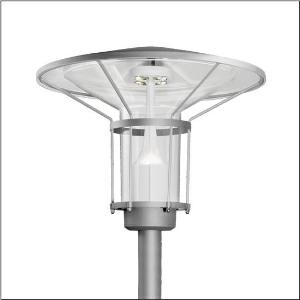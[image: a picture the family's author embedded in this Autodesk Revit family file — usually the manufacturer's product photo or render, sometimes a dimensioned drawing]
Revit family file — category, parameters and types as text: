
# Revit family: laterne_classic_iq___p1_0a_5xa5245ff14h_a382
name_source: partatom
category: Lighting Fixtures
units: mm (PartAtom-declared; Revit-internal decimal feet)

## family parameters
Cut with Voids When Loaded = No
Host = Face
Light Source = No
Part Type = Normal
Room Calculation Point = No
Round Connector Dimension = Use Diameter
Shared = No

## types (1)
- --- (1 x LED, 1360 lm, 10.5 W, 3000K)
    Apparent Load = 11 VA
    CIE Flux Codes = 30 61 91 96 100
    Color Rendering = 70
    Color Temperature = 3000K
    Default Elevation = 1800 mm
    Description = Lantern Classic iQ, mast luminaire, Module 540 iQ-SR, primary light control with 3 zone facetted reflector, of plastic, silver coated, highly specular, structured, primary optical cover: cover, of PMMA, transparent, light distribution: P1.0a, light emission: direct distribution, primary light characteristic: strongly asymmetric, installation type: post-top, LED, High Power LED, rated luminous flux: 1.360lm, luminous efficacy: 130lm/W, light colour: 730, colour temperature: 3000K, control gear: ECG iQ, control: Auto-Match, Temp-Guard, Lumen-Switch, Night-Set, Smart-Wire, Light-Fading, Desk-Remote (wireless, voltage-free reading and setting of iQ features in the workshop via application-optimized NFC function/RFID function), optimised constant luminous flux control (CLO 2.0), Street-Remote, presetting dimming logarithmic, with terminal, 6-pole, max. 2.5mm², mains connection: 230..240V, AC, 50/60Hz, start of lifetime: 11W, end of service life: 11W, reduction: 5W, luminaire housing, upper part, of glass-fibre reinforced polyester, coated, Siteco® metallic grey (DB 702S), diameter: 750mm, height: 596mm, spigot size: d x l = 76 x 70mm (post-top) | with reducer (optional accessory) 60 x 70mm, post-top mast mounting element, of diecast aluminium, coated, Siteco® metallic grey (DB 702S), Module 540 iQ-SR, traffic white (RAL 9016), equipment: standard, protection rating (complete): IP65, insulation class (complete): insulation class II (safety insulation), certification: CE, ENEC, VDE, packaging unit: 1 piece

Light Distribution: P1.0a
    Height = 596 mm
    Lamp = 1 x LED
    Lamp Light Flux = 1360 lm
    Lamp Power = 10.5 W
    Lamp count = 1
    Length = 750 mm
    Luminous efficacy = 130 lm/W
    Manufacturer = Siteco
    ModVariant = No
    Model = 5XA5245FF14H
    Number of Poles = 1
    OnlyDefault = Yes
    Power Factor = 1
    Product Name = Laterne Classic iQ | P1.0a
    Product group = mast luminaire | pylon top
    ProductGroupID = 6100
    Protection Class = Protection class II
    Protection Degree = IP 65
    RLX_Detail_Level = 1
    RLX_Emergency_Light_Flux = 0 lm
    RLX_Emergency_Type = 0
    RLX_Emergency_Type_DB = No
    RlxData = <blob elided: 93937 chars, md5=b58ff5dd>
    Socket = socket
    Standby Power = 0 W
    System Light Flux = 1360 lm
    System Power = 11 W
    Type Comments = factory setting: luminous flux: 100 % | dim-lin: 254 | 419 mA
    Type Image = l_1006052.jpg
    URL = http://relux.com
    VarID = @adj_092569
    Voltage = 0 V
    Weight = 0.00 kg
    Width = 0 mm  [stored 0 ft]

note: [stored X ft] marks values corroborated as IEEE doubles in the binary element streams (Revit-internal decimal feet)

## geometry (parser evidence)
native form markers: Blend x4, Sweep x10
no freeform markers — native parametric forms only
